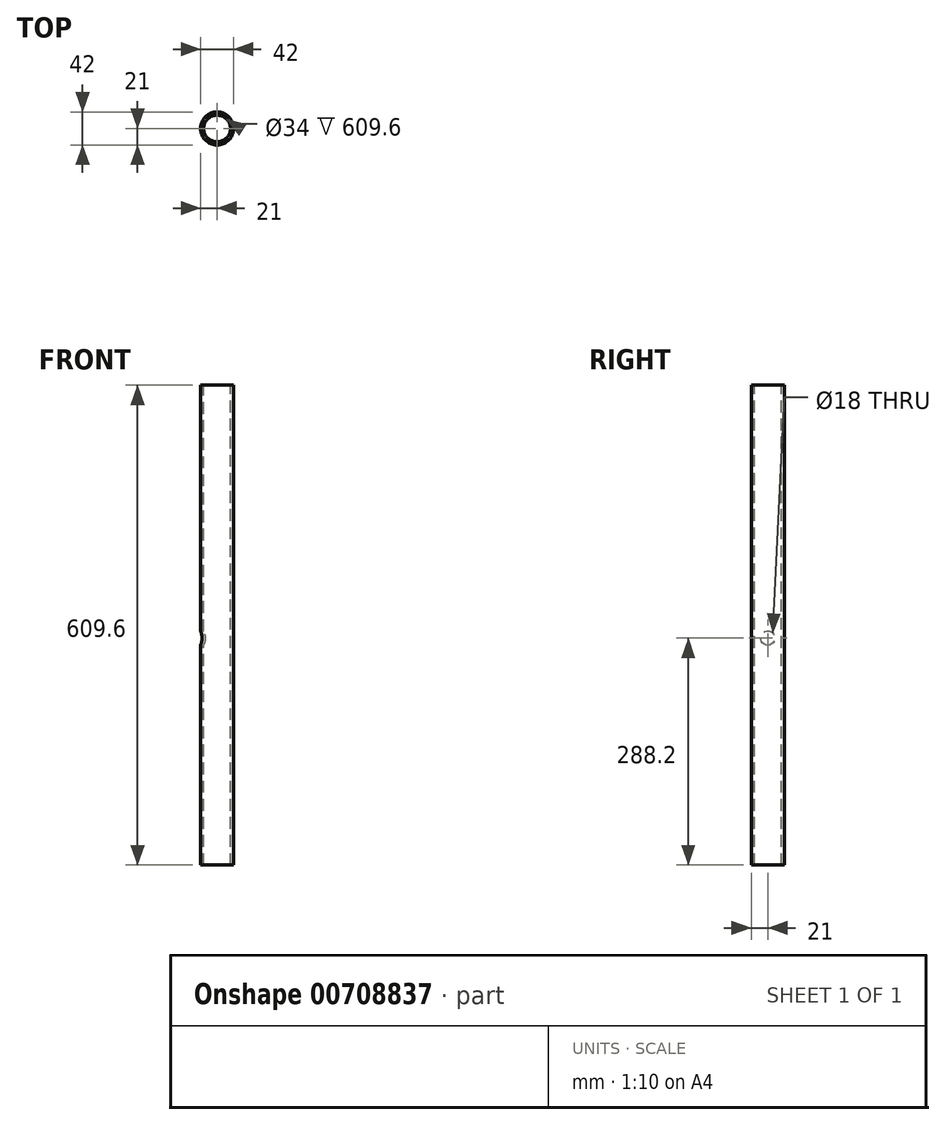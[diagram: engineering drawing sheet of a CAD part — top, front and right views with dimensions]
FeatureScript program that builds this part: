
annotation { "Feature Type Name" : "Feature", "Feature Type Description" : "" }
export const myFeature = defineFeature(function(context is Context, id is Id, definition is map)
    precondition{}
    {
        {
            var Q0;
            Q0=qCreatedBy(makeId("Front.planeOp"),FACE);
            var sketch = newSketch(context, id + "F0", { "sketchPlane" : qUnion([Q0])});
            skLineSegment(sketch, "E0", {"start": v(0, 270.85) * mm, "end": v(0, -338.75) * mm});
            skLineSegment(sketch, "E1", {"start": v(21, 271.4) * mm, "end": v(21, -338.2) * mm});
            skLineSegment(sketch, "E2", {"start": v(21, -338.2) * mm, "end": v(17, -338.2) * mm});
            skLineSegment(sketch, "E3", {"start": v(17, -338.2) * mm, "end": v(17, 271.4) * mm});
            skLineSegment(sketch, "E4", {"start": v(21, 271.4) * mm, "end": v(17, 271.4) * mm});
            skSolve(sketch);
        }
        {
            var Q0;
            Q0 = qSketchRegion(id + "F0", true);
            var Q1;
            Q1=sQuery(id+"F0.wireOp",EDGE,"E0");
            revolve(context, id + "F1", {"surfaceOperationType" : NewSurfaceOperationType.NEW, "entities" : qUnion([Q0]), "axis" : qUnion([Q1]), "revolveType" : RevolveType.FULL});
        }
        {
            var Q0;
            Q0=qCreatedBy(makeId("Right.planeOp"),FACE);
            var sketch = newSketch(context, id + "F2", { "sketchPlane" : qUnion([Q0])});
            skCircle(sketch, "E5", {"center": v(0, -50) * mm, "radius": 9 * mm});
            skSolve(sketch);
        }
        {
            var Q0;
            Q0 = qSketchRegion(id + "F2", true);
            extrude(context, id + "F3", {"entities" : qUnion([Q0]), "operationType" : NewBodyOperationType.REMOVE, "endBound" : BoundingType.THROUGH_ALL, "oppositeDirection" : true, "depth" : 25 * mm, "offsetDistance" : 25 * mm});
        }
    });
